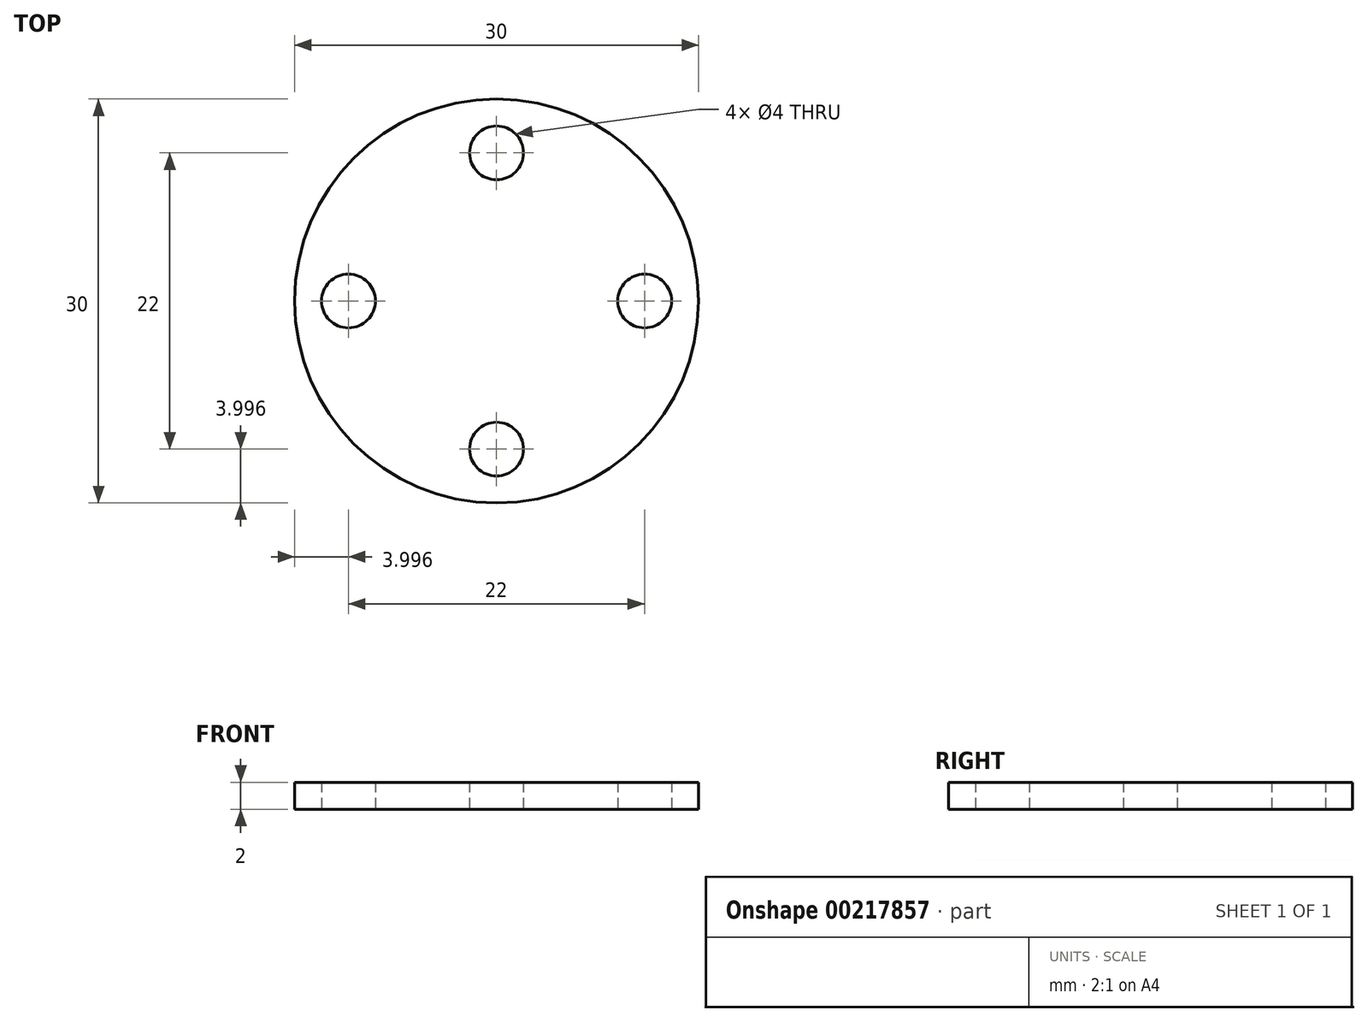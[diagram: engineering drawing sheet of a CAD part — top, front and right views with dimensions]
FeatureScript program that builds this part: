
annotation { "Feature Type Name" : "Feature", "Feature Type Description" : "" }
export const myFeature = defineFeature(function(context is Context, id is Id, definition is map)
    precondition{}
    {
        {
            var Q0;
            Q0=qCreatedBy(makeId("Top.planeOp"),FACE);
            var sketch = newSketch(context, id + "F0", { "sketchPlane" : qUnion([Q0])});
            skCircle(sketch, "E0", {"center": v(15.6, -35.28) * mm, "radius": 2 * mm});
            skCircle(sketch, "E1", {"center": v(15.6, -13.28) * mm, "radius": 2 * mm});
            skCircle(sketch, "E2", {"center": v(4.6, -24.28) * mm, "radius": 2 * mm});
            skCircle(sketch, "E3", {"center": v(26.6, -24.28) * mm, "radius": 2 * mm});
            skCircle(sketch, "E4", {"center": v(15.6, -24.28) * mm, "radius": 15 * mm});
            skSolve(sketch);
        }
        {
            var Q0;
            Q0=makeQuery(id+"F0.imprint","IMPRINT",FACE,{"disambiguationData":[TD([[makeQuery(id+"F0.imprint","IMPRINT",EDGE,{"derivedFrom":sQuery(id+"F0.wireOp",EDGE,"E0")}),-1.0]])]});
            extrude(context, id + "F1", {"entities" : qUnion([Q0]), "depth" : 2 * mm});
        }
    });
